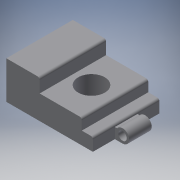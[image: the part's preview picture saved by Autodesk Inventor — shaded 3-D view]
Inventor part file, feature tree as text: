
AUTODESK INVENTOR PART (.ipt)
format: ipt  version: 2016 (Build 200138000, 138)  size: 299,520 bytes
history: native  units: in
note: dims shown in document units (in); Inventor stores cm internally (conversion verified against a paired STEP export)
features: extrude x20, sketch x18, reference x8, projected_geometry x6, plane x2, fillet x1
ambient origin geometry x8: Origin, YZ Plane, XZ Plane, XY Plane, X Axis, Y Axis, Z Axis, Center Point
bodies: Solid1 (feature_tree)
feature tree (55):
  extrude  "Extrusion1"  Depth=0.05in
  plane  "Work Plane1"
  extrude  "Extrusion5"  Depth=0.2362in
  plane  "Work Plane3"
  extrude  "Extrusion6"  [1 undecoded]
  extrude  "Extrusion8"  [1 undecoded]
  extrude  "Extrusion9"  Depth=0.4in TaperAngle=0.0deg
  extrude  "Extrusion10"  Depth=0.4in TaperAngle=0.0deg
  extrude  "Extrusion11"  Depth=0.3937in
  extrude  "Extrusion12"  Depth=0.05in TaperAngle=0.0deg
  extrude  "Extrusion13"  Depth=0.3937in TaperAngle=0.0deg
  extrude  "Extrusion14"  Depth=0.3937in TaperAngle=0.0deg
  extrude  "Extrusion15"  Depth=0.1969in TaperAngle=0.0deg
  extrude  "Extrusion16"  Depth=0.4724in
  extrude  "Extrusion17"  Depth=0.0197in
  extrude  "Extrusion18"  Depth=0.0394in TaperAngle=0.0deg
  extrude  "Extrusion19"  Depth=0.0394in
  extrude  "Extrusion20"  Depth=0.001in TaperAngle=0.0deg
  extrude  "Extrusion21"  [1 undecoded]
  extrude  "Extrusion22"  [1 undecoded]
  fillet  "Fillet1"  [1 undecoded]
  extrude  "Extrusion23"  [1 undecoded]
  extrude  "Extrusion24"  [1 undecoded]
  sketch  "Sketch1"  dims[d0=0.15in d1=0.05in]
  sketch  "Sketch2"  dims[d2=0.2362in d3=0.1496in]
  sketch  "Sketch6"  dims[d4=1.2in d5=0.0in d6=-0.4in]
  sketch  "Sketch8"  dims[d19=1.0in d20=0.0in d21=-0.4in]
  sketch  "Sketch9"  dims[d22=1.0in d23=0.0in d26=0.4in d27=0.0in]
  projected_geometry  "Projected Loop1"
  sketch  "Sketch10"  dims[d28=0.4in d29=0.0in d30=0.4in d31=0.0in]
  sketch  "Sketch11"  dims[d32=0.4in d33=0.0in d34=0.3937in]
  sketch  "Sketch12"  dims[d35=0.05in d36=0.0in d37=0.05in d38=0.0in]
  sketch  "Sketch13"  dims[d39=0.1772in d40=0.3937in d41=0.0in]
  reference  "Reference1"
  reference  "Reference2"
  sketch  "Sketch15"  dims[d42=0.0098in d43=0.3937in d44=0.0in]
  sketch  "Sketch16"  dims[d45=0.3937in d46=0.0in d47=0.1969in d48=0.0in]
  projected_geometry  "Projected Loop2"
  sketch  "Sketch17"  dims[d49=1.1801in d50=0.0in d51=0.4724in]
  reference  "Reference3"
  sketch  "Sketch18"  dims[d52=1.1801in d53=0.0in d54=0.0197in]
  reference  "Reference4"
  reference  "Reference5"
  reference  "Reference6"
  reference  "Reference7"
  sketch  "Sketch20"  dims[d55=23.0in d56=0.0in d57=0.0394in d58=0.0in]
  sketch  "Sketch21"  dims[d59=0.0394in d60=0.0in d61=0.0394in]
  projected_geometry  "Projected Loop3"
  sketch  "Sketch22"  dims[d62=0.001in d63=0.0in d64=0.001in d65=0.0in]
  sketch  "Sketch23"
  reference  "Reference8"
  projected_geometry  "Projected Loop4"
  projected_geometry  "Projected Loop5"
  sketch  "Sketch24"
  projected_geometry  "Projected Loop6"
note: 7 required parameter values undecoded (feature->parameter linkage not recoverable at this tier; creation-order binding heuristic only, values carry confidence <= 0.55)
